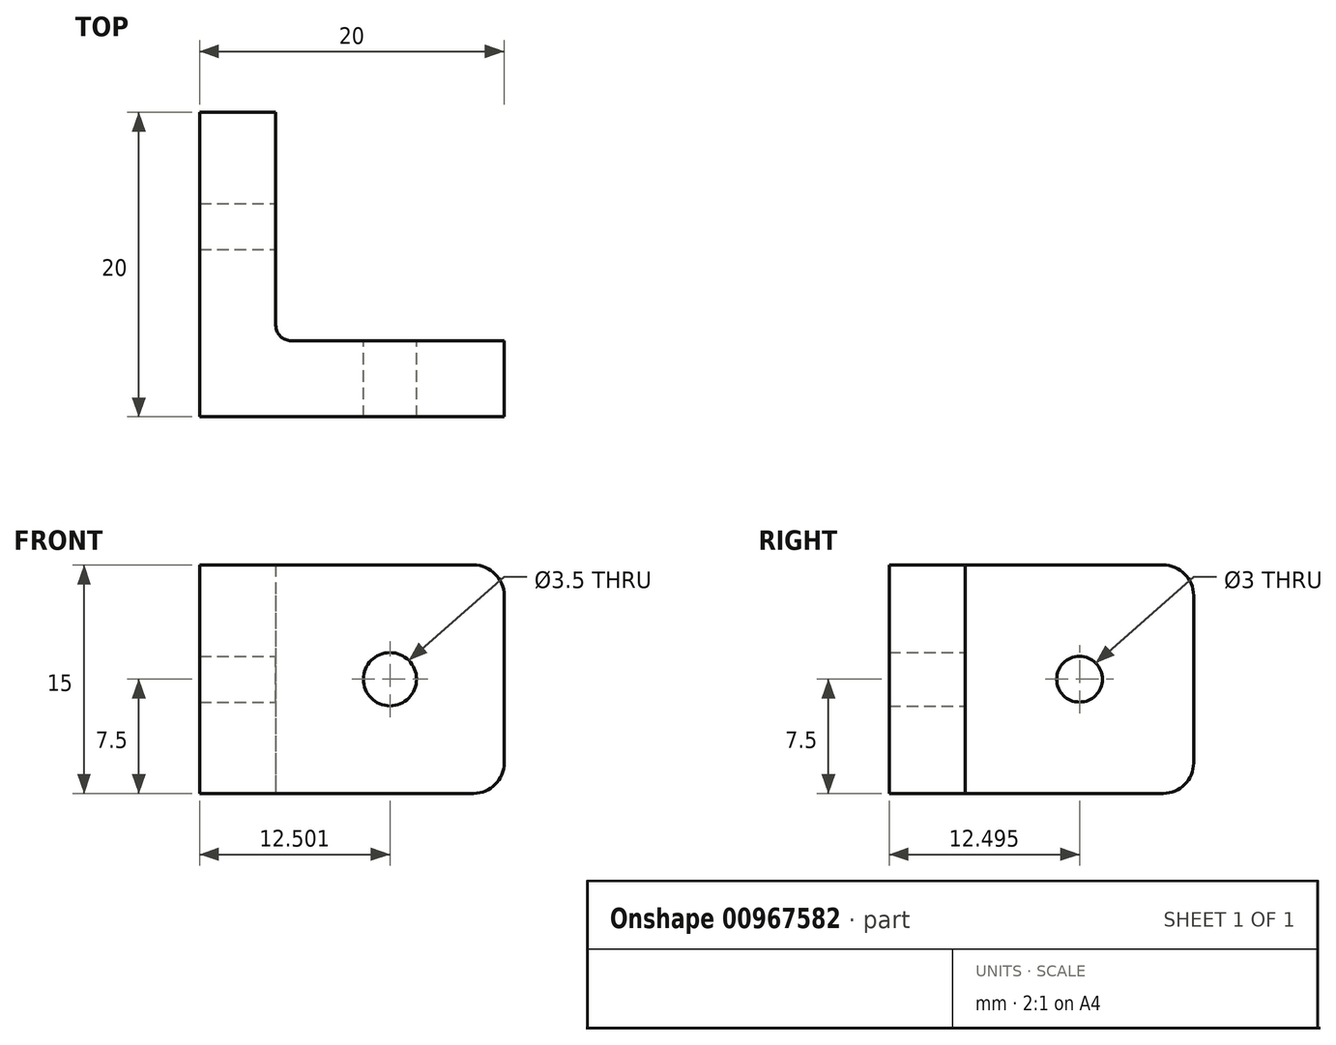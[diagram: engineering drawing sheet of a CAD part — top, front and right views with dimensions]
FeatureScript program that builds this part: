
annotation { "Feature Type Name" : "Feature", "Feature Type Description" : "" }
export const myFeature = defineFeature(function(context is Context, id is Id, definition is map)
    precondition{}
    {
        {
            var Q0;
            Q0=qCreatedBy(makeId("Top.planeOp"),FACE);
            var sketch = newSketch(context, id + "F0", { "sketchPlane" : qUnion([Q0])});
            skLineSegment(sketch, "E0.bottom", {"start": v(-7695.7, 2860.87) * mm, "end": v(-7690.7, 2860.87) * mm});
            skLineSegment(sketch, "E0.top", {"start": v(-7695.7, 2880.87) * mm, "end": v(-7690.7, 2880.87) * mm});
            skLineSegment(sketch, "E0.left", {"start": v(-7695.7, 2860.87) * mm, "end": v(-7695.7, 2880.87) * mm});
            skLineSegment(sketch, "E0.right", {"start": v(-7690.7, 2860.87) * mm, "end": v(-7690.7, 2880.87) * mm});
            skLineSegment(sketch, "E1.bottom", {"start": v(-7690.7, 2860.87) * mm, "end": v(-7675.7, 2860.87) * mm});
            skLineSegment(sketch, "E1.top", {"start": v(-7690.7, 2865.87) * mm, "end": v(-7675.7, 2865.87) * mm});
            skLineSegment(sketch, "E1.left", {"start": v(-7690.7, 2860.87) * mm, "end": v(-7690.7, 2865.87) * mm});
            skLineSegment(sketch, "E1.right", {"start": v(-7675.7, 2860.87) * mm, "end": v(-7675.7, 2865.87) * mm});
            skSolve(sketch);
        }
        {
            var Q0;
            Q0 = qSketchRegion(id + "F0", true);
            extrude(context, id + "F1", {"entities" : qUnion([Q0]), "depth" : 15 * mm, "offsetDistance" : 25.4 * mm});
        }
        {
            var Q0;
            Q0=makeQuery(id+"F1.opExtrude","SWEPT_FACE",FACE,{"disambiguationData":[OSD([sQuery(id+"F0.wireOp",EDGE,"E1.top")])]});
            var sketch = newSketch(context, id + "F2", { "sketchPlane" : qUnion([Q0])});
            skCircle(sketch, "E2", {"center": v(7683.2, 7.5) * mm, "radius": 1.5 * mm});
            skPoint(sketch, "E2.centerSnap0", {"position": v(7683.2, 15) * mm});
            skPoint(sketch, "E2.centerSnap1", {"position": v(7690.7, 7.5) * mm});
            skSolve(sketch);
        }
        {
            var Q0;
            Q0=makeQuery(id+"F1.opExtrude","SWEPT_FACE",FACE,{"disambiguationData":[OSD([sQuery(id+"F0.wireOp",EDGE,"E0.right")])]});
            var sketch = newSketch(context, id + "F3", { "sketchPlane" : qUnion([Q0])});
            skCircle(sketch, "E3", {"center": v(2873.37, 7.5) * mm, "radius": 1.5 * mm});
            skPoint(sketch, "E3.centerSnap0", {"position": v(2865.87, 7.5) * mm});
            skPoint(sketch, "E3.centerSnap1", {"position": v(2873.37, 15) * mm});
            skSolve(sketch);
        }
        {
            var Q0;
            Q0 = qSketchRegion(id + "F3", true);
            extrude(context, id + "F4", {"entities" : qUnion([Q0]), "operationType" : NewBodyOperationType.REMOVE, "oppositeDirection" : true, "depth" : 127 * mm, "offsetDistance" : 25.4 * mm});
        }
        {
            var Q0;
            Q0=sQuery(id+"F2.wireOp",VERTEX,"E2.center");
            var Q1;
            Q1=makeQuery(id+"F1.opExtrude","SWEPT_BODY",BODY,{"disambiguationData":[OSD([sQuery(id+"F0.wireOp",EDGE,"E0.bottom"),sQuery(id+"F0.wireOp",EDGE,"E0.top"),sQuery(id+"F0.wireOp",EDGE,"E0.left"),sQuery(id+"F0.wireOp",EDGE,"E0.right"),sQuery(id+"F0.wireOp",EDGE,"E1.bottom"),sQuery(id+"F0.wireOp",EDGE,"E1.top"),sQuery(id+"F0.wireOp",EDGE,"E1.right")])]});
            hole(context, id + "F5", {"style" : HoleStyle.SIMPLE, "endStyle" : HoleEndStyle.THROUGH, "holeDiameter" : 3.5 * mm, "majorDiameter" : 6.35 * mm, "isTappedThrough" : true, "tappedDepth" : 12.7 * mm, "tapClearance" : 3, "startFromSketch" : true, "locations" : qUnion([Q0]), "scope" : qUnion([Q1])});
        }
        {
            var Q0;
            Q0=makeQuery(id+"F1.opExtrude","CAP_EDGE",EDGE,{"disambiguationData":[OSD([sQuery(id+"F0.wireOp",EDGE,"E0.top")])],"isStart":false});
            var Q1;
            Q1=makeQuery(id+"F1.opExtrude","CAP_EDGE",EDGE,{"disambiguationData":[OSD([sQuery(id+"F0.wireOp",EDGE,"E0.top")])],"isStart":true});
            fillet(context, id + "F6", {"entities" : qUnion([Q0, Q1]), "radius" : 2 * mm, "tangentPropagation" : true, "allowEdgeOverflow" : false});
        }
        {
            var Q0;
            Q0=makeQuery(id+"F1.opExtrude","CAP_EDGE",EDGE,{"disambiguationData":[OSD([sQuery(id+"F0.wireOp",EDGE,"E1.right")])],"isStart":false});
            var Q1;
            Q1=makeQuery(id+"F1.opExtrude","CAP_EDGE",EDGE,{"disambiguationData":[OSD([sQuery(id+"F0.wireOp",EDGE,"E1.right")])],"isStart":true});
            fillet(context, id + "F7", {"entities" : qUnion([Q0, Q1]), "radius" : 2 * mm, "tangentPropagation" : true, "allowEdgeOverflow" : false});
        }
        {
            var Q0;
            Q0=makeQuery(id+"F1.opExtrude","SWEPT_EDGE",EDGE,{"disambiguationData":[OSD([sQuery(id+"F0.wireOp",EDGE,"E0.right"),sQuery(id+"F0.wireOp",EDGE,"E1.top"),sQuery(id+"F0.wireOp",EDGE,"E1.left")])]});
            fillet(context, id + "F8", {"entities" : qUnion([Q0]), "radius" : 1 * mm, "tangentPropagation" : true, "allowEdgeOverflow" : false});
        }
    });
